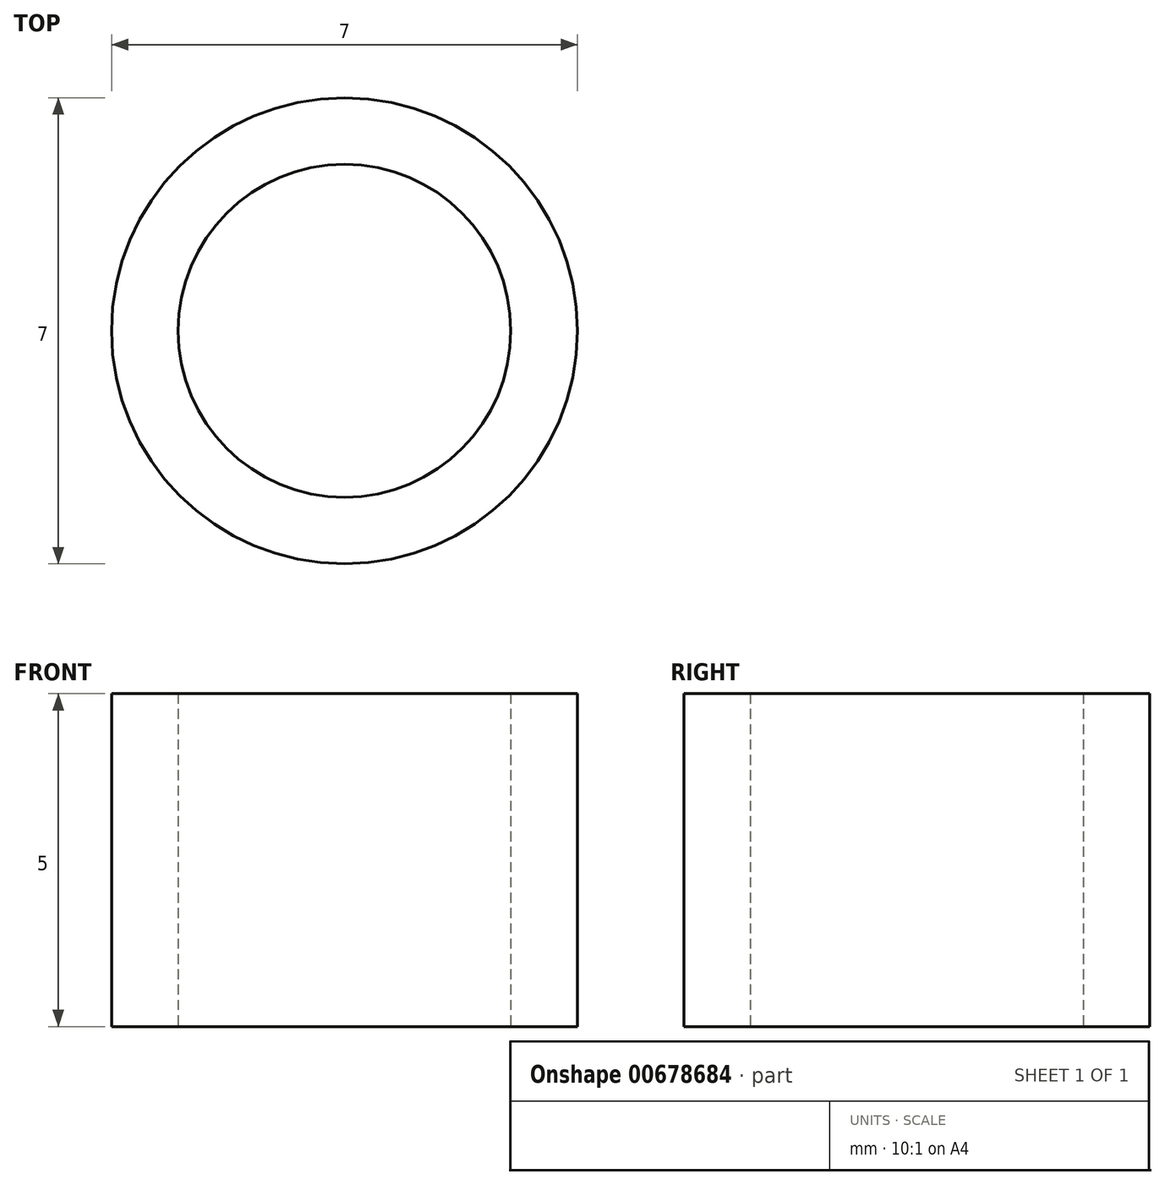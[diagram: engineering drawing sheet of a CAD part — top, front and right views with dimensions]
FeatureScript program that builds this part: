
annotation { "Feature Type Name" : "Feature", "Feature Type Description" : "" }
export const myFeature = defineFeature(function(context is Context, id is Id, definition is map)
    precondition{}
    {
        {
            var Q0;
            Q0=qCreatedBy(makeId("Top.planeOp"),FACE);
            var sketch = newSketch(context, id + "F0", { "sketchPlane" : qUnion([Q0])});
            skCircle(sketch, "E0", {"center": v(0, 0) * mm, "radius": 2.5 * mm});
            skCircle(sketch, "E1", {"center": v(0, 0) * mm, "radius": 3.5 * mm});
            skSolve(sketch);
        }
        {
            var Q0;
            Q0 = qSketchRegion(id + "F0", true);
            extrude(context, id + "F1", {"entities" : qUnion([Q0]), "depth" : 5 * mm, "offsetDistance" : 25 * mm});
        }
    });
